# Revit family: Shower-Wall_Supply_Elbow-KOHLER-RENEW-K-98351T_1
name_source: partatom
category: Plumbing Fixtures
revit_build: Autodesk Revit 2017 (Build: 20160225_1515(x64)
units: mm (PartAtom-declared; Revit-internal decimal feet)

## family parameters
Cut with Voids When Loaded = No
Host = Face
OmniClass Number = 23.31.17.00
OmniClass Title = Showers
Part Type = Normal
Room Calculation Point = No
Round Connector Dimension = Use Diameter
Shared = No

## types (6) — shared parameters
ADA Compliant = No
Assembly Code = D2010700
CW Connection = No
Cold Water Inlet = Cold Water Inlet
Date Modified = 06/23/2020
Default Elevation = 36"
Description = Oxygen wall connector
Drain Included = No
Flow Rate = 0 GPM
HW Connection = Yes
Height = 2 5/16"
Hot Water Inlet = Hot Water Inlet
Length = 2 5/16"
Manufacturer = KOHLER Co.
Master Format 2014 = 22 42 23
Master Format 2014 Name = Residential Showers
Material = Premium Metal Construction
Panel Thickness = 0"
Pressure = 0.00 psi
Product Documentation Link = https://files.kohler.com.cn
Product Name = RENEW
Product Page URL = https://www.kohler.com.cn
Tempered Water Inlet = Tempered Water Inlet
URL = http://www.kohler.com.cn
Vent Connection = No
Waste Connection = No
Waste Water Outlet = Waste Water Outlet
WaterSense Certified = No
Width = 2"

## per-type parameters (varying)
| type | Finish | Model | Type |
| CP-Polished Chrome | Kohler-Metal-CP-Polished_Chrome | K-98351T-CP | 1 |
| 2BL-Original Black | Kohler-Metal-2BL-Original_Black | K-98351T-2BL | 2 |
| AF-Flange Gold | Kohler-Metal-AF-Flange_Gold | K-98351T-AF | 3 |
| BN-Roman Silver | Kohler-Metal-BN-Roman_Silver | K-98351T-BN | 4 |
| RGD-Rose Gold | Kohler-Metal-RGD-Rose_Gold | K-98351T-RGD | 5 |
| BL-Primary Black | Kohler-Metal-BL-Matte_Black | K-98351T-BL | 6 |

## geometry (parser evidence)
native form markers: Sweep x5
no freeform markers — native parametric forms only
